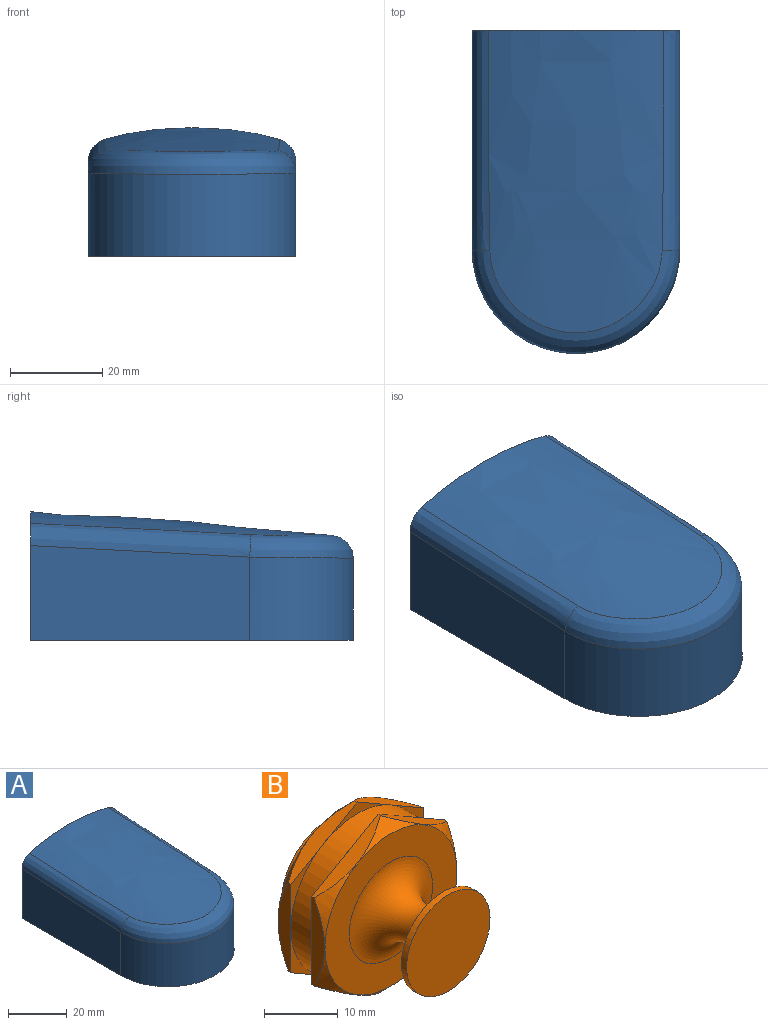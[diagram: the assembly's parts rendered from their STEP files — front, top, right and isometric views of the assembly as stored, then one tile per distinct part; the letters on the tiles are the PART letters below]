
ASSEMBLY  parts=2 mates=1
PART A: 24 faces, bbox 51x84.5x33.9 mm
  f0: plane 45.11x28mm, normal (0,1,0), area 134.6mm2, adj f1,f2,f3,f4,f6,f8,f9,f10
  f1: plane 70x45mm, normal (0,0,-1), area 593.3mm2, adj f0,f2,f4,f5,f9,f10,f15,f16
  f2: plane 47.5x20.54mm, normal (1,0,0), area 918.7mm2, adj f0,f1,f5,f6
  f3: bspline ~70x45mm, area 2332.5mm2, adj f0,f6,f7,f8
  f4: plane 47.5x20.54mm, normal (-1,0,0), area 918.7mm2, adj f0,f1,f5,f8
  f5: cylinder r=22.5mm len=45mm, axis (0,0,-1), area 1274.7mm2, adj f1,f2,f4,f7
  f6: bspline ~66.49x8.37mm, area 305.9mm2, adj f0,f2,f3,f7
  f7: bspline ~45.01x25.02mm, area 467.2mm2, adj f3,f5,f6,f8
  f8: bspline ~66.49x8.37mm, area 305.9mm2, adj f0,f3,f4,f7
  f9: plane 20.54x3mm, normal (-0.97,0.26,0), area 63.8mm2, adj f0,f1,f14,f15
  f10: plane 20.54x3mm, normal (0.97,0.26,0), area 63.8mm2, adj f0,f1,f11,f15
  f11: bspline ~3.6x3.36mm, area 12.4mm2, adj f0,f10,f12,f15
  f12: bspline ~18.49x3.26mm, area 57.8mm2, adj f0,f11,f13,f15
  f13: bspline ~18.49x3.6mm, area 57.8mm2, adj f0,f12,f14,f15
  f14: bspline ~3.6x3.36mm, area 12.4mm2, adj f0,f9,f13,f15
  f15: plane 40.4x25.59mm, normal (0,1,0), area 993.1mm2, adj f1,f9,f10,f11,f12,f13,f14
  f16: plane 41.5x20.25mm, normal (-1,0,0), area 796.3mm2, adj f1,f19,f20,f23
  f17: offset ~76x51mm, area 1512.1mm2, adj f20,f21,f22,f23
  f18: plane 41.5x20.25mm, normal (1,0,0), area 796.3mm2, adj f1,f19,f22,f23
  f19: cylinder r=19.5mm len=39mm, axis (0,0,-1), area 1104.7mm2, adj f1,f16,f18,f21
  f20: bspline ~58.66x5.11mm, area 106.7mm2, adj f16,f17,f21,f23
  f21: bspline ~39.01x21.69mm, area 168.8mm2, adj f17,f19,f20,f22
  f22: bspline ~58.66x5.11mm, area 106.7mm2, adj f17,f18,f21,f23
  f23: plane 42.08x27.64mm, normal (0,-1,0), area 922.5mm2, adj f1,f16,f17,f18,f20,f22
PART B: 36 faces, bbox 29.3x23x29.3 mm
  f0: plane 12.7x7.33mm, normal (0.5,0,-0.87), area 26.3mm2, adj f1,f5,f10,f13,f15
  f1: plane 12.7x7.33mm, normal (-0.5,0,-0.87), area 26.3mm2, adj f0,f2,f10,f12,f13
  f2: plane 14.69x2.48mm, normal (-1,0,0), area 26.3mm2, adj f1,f3,f10,f11,f12
  f3: plane 12.7x7.33mm, normal (-0.5,0,0.87), area 26.3mm2, adj f2,f4,f10,f11,f14
  f4: plane 12.7x7.33mm, normal (0.5,0,0.87), area 26.3mm2, adj f3,f5,f10,f14,f22
  f5: plane 14.69x2.48mm, normal (1,0,0), area 26.3mm2, adj f0,f4,f10,f15,f22
  f6: plane 25.33x25.33mm, normal (0,-1,0), area 302.8mm2, adj f8,f10
  f7: plane 16x16mm, normal (0,-1,0), area 201.1mm2, adj f9
  f8: torus R=8mm, axis (0,-1,0), area 475.4mm2, adj f6,f9
  f9: cylinder r=8mm len=16mm, axis (0,-1,0), area 50.3mm2, adj f7,f8
  f10: cone r=12.66mm half-angle=45deg, axis (0,1,0), area 77.5mm2, adj f0,f1,f2,f3,f4,f5,f6
  f11: plane 11x6.35mm, normal (0,1,0), area 8.7mm2, adj f2,f3,f16
  f12: plane 11x6.35mm, normal (0,1,0), area 8.7mm2, adj f1,f2,f16
  f13: plane 12.7x3.67mm, normal (0,1,0), area 8.7mm2, adj f0,f1,f16
  f14: plane 12.7x3.67mm, normal (0,1,0), area 8.7mm2, adj f3,f4,f16
  f15: plane 11x6.35mm, normal (0,1,0), area 8.7mm2, adj f0,f5,f16
  f16: cylinder r=12.7mm len=25.4mm, axis (0,-1,0), area 319.2mm2, adj f11,f12,f13,f14,f15,f17,f18,f19
  f17: plane 11x6.35mm, normal (0,-1,0), area 8.7mm2, adj f16,f30,f31
  f18: plane 11x6.35mm, normal (0,-1,0), area 8.7mm2, adj f16,f31,f32
  f19: plane 12.7x3.67mm, normal (0,-1,0), area 8.7mm2, adj f16,f32,f33
  f20: plane 12.7x3.67mm, normal (0,-1,0), area 8.7mm2, adj f16,f29,f30
  f21: plane 11x6.35mm, normal (0,-1,0), area 8.7mm2, adj f16,f28,f33
  f22: plane 11x6.35mm, normal (0,1,0), area 8.7mm2, adj f4,f5,f16
  f23: plane 11x6.35mm, normal (0,-1,0), area 8.7mm2, adj f16,f28,f29
  f24: plane 18x18mm, normal (0,1,0), area 197.7mm2, adj f25,f35
  f25: cylinder r=9mm len=18mm, axis (0,-1,0), area 169.6mm2, adj f24,f26
  f26: plane 25.33x25.33mm, normal (0,1,0), area 249.4mm2, adj f25,f27
  f27: cone r=12.66mm half-angle=45deg, axis (0,-1,0), area 77.5mm2, adj f26,f28,f29,f30,f31,f32,f33
  f28: plane 14.69x2.48mm, normal (1,0,0), area 26.3mm2, adj f21,f23,f27,f29,f33
  f29: plane 12.7x7.33mm, normal (0.5,0,0.87), area 26.3mm2, adj f20,f23,f27,f28,f30
  f30: plane 12.7x7.33mm, normal (-0.5,0,0.87), area 26.3mm2, adj f17,f20,f27,f29,f31
  f31: plane 14.69x2.48mm, normal (-1,0,0), area 26.3mm2, adj f17,f18,f27,f30,f32
  f32: plane 12.7x7.33mm, normal (-0.5,0,-0.87), area 26.3mm2, adj f18,f19,f27,f31,f33
  f33: plane 12.7x7.33mm, normal (0.5,0,-0.87), area 26.3mm2, adj f19,f21,f27,f28,f32
  f34: cone r=0mm half-angle=59deg, axis (0,1,0), area 66.2mm2, adj f35
  f35: cylinder r=4.25mm len=10mm, axis (0,1,0), area 267mm2, adj f24,f34
PLACE A t=(-90.83,-202.2,56.15)mm
PLACE B rot(axis=(-1,0,0),90deg) t=(-91.68,-225.4,39.15)mm
MATE planar B.f25 <-> A.f1  axis (0,0,-1) through (-91.68,-225.4,36.15)mm
